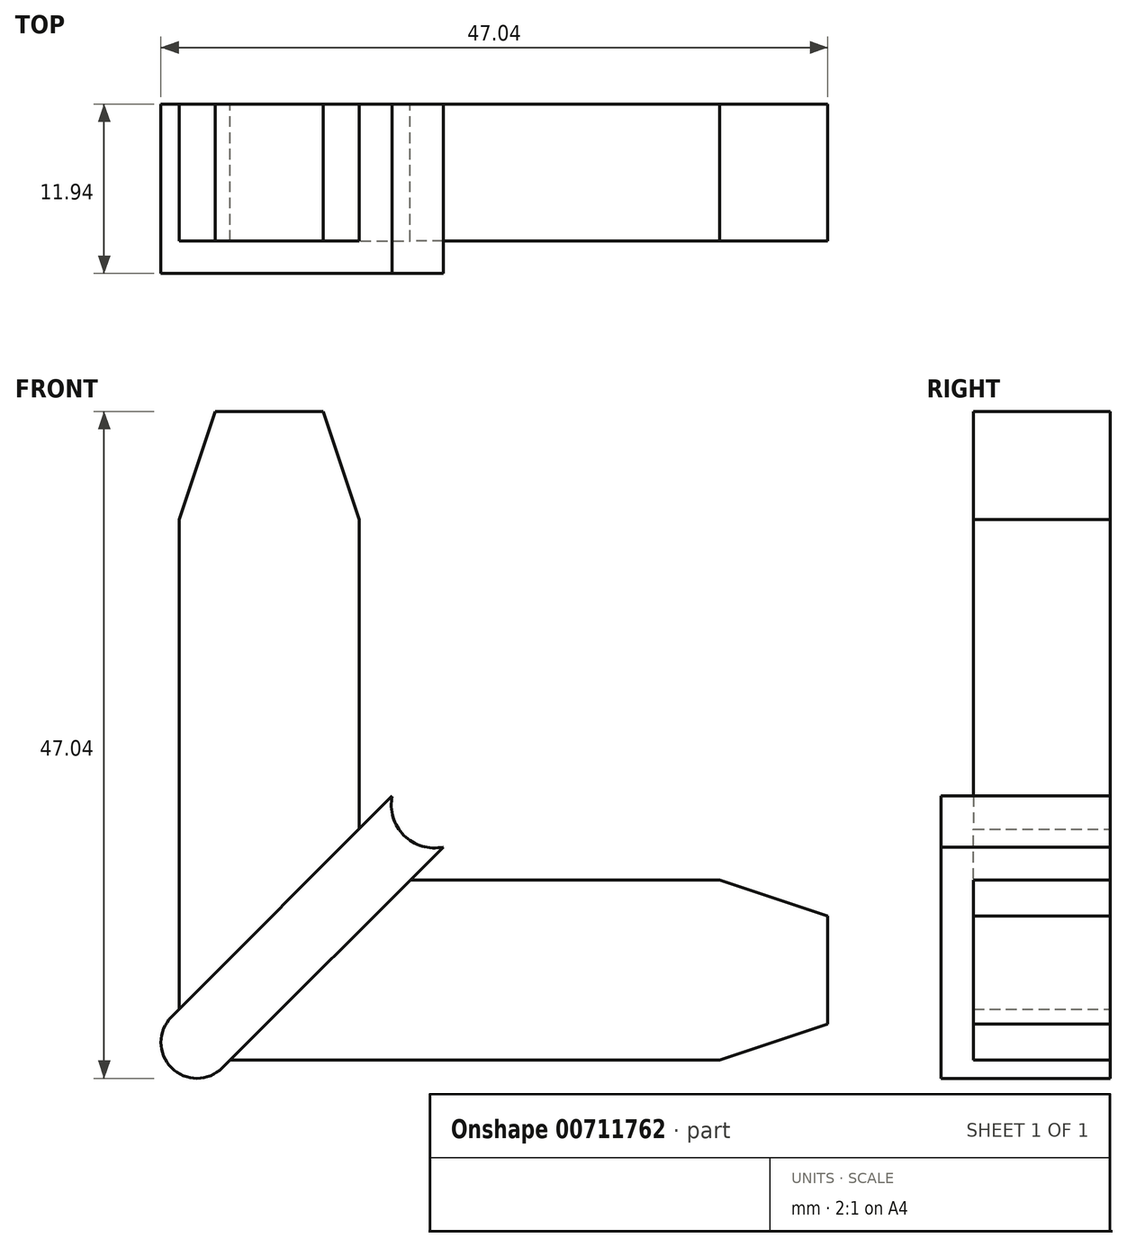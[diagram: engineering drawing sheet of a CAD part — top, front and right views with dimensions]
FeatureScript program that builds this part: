
annotation { "Feature Type Name" : "Feature", "Feature Type Description" : "" }
export const myFeature = defineFeature(function(context is Context, id is Id, definition is map)
    precondition{}
    {
        {
            var Q0;
            Q0=qCreatedBy(makeId("Front.planeOp"),FACE);
            var sketch = newSketch(context, id + "F0", { "sketchPlane" : qUnion([Q0])});
            skLineSegment(sketch, "E0.bottom", {"start": v(-4.55, -8.15) * mm, "end": v(37.61, -8.15) * mm});
            skLineSegment(sketch, "E0.right", {"start": v(37.61, -8.15) * mm, "end": v(37.61, 0) * mm});
            skPoint(sketch, "E0.middle", {"position": v(27.24, 0) * mm});
            skLineSegment(sketch, "E1.bottom", {"start": v(-6.89, -10.48) * mm, "end": v(10.48, 6.89) * mm});
            skLineSegment(sketch, "E1.top", {"start": v(-10.48, -6.89) * mm, "end": v(6.89, 10.48) * mm});
            skLineSegment(sketch, "E1.left", {"start": v(-6.89, -10.48) * mm, "end": v(-10.48, -6.89) * mm});
            skLineSegment(sketch, "E1.right", {"start": v(10.48, 6.89) * mm, "end": v(6.89, 10.48) * mm});
            skPoint(sketch, "E1.middle", {"position": v(0, 0) * mm});
            skLineSegment(sketch, "E2", {"start": v(0, 0) * mm, "end": v(15.93, 15.93) * mm, "construction": true});
            skLineSegment(sketch, "E3", {"start": v(37.61, 0) * mm, "end": v(37.61, 4.55) * mm});
            skLineSegment(sketch, "E4", {"start": v(37.61, 4.55) * mm, "end": v(8.15, 4.55) * mm});
            skLineSegment(sketch, "E5.MirrorCS", {"start": v(4.55, 37.61) * mm, "end": v(4.55, 8.15) * mm});
            skLineSegment(sketch, "E6.MirrorCS", {"start": v(-8.15, 37.61) * mm, "end": v(0, 37.61) * mm});
            skLineSegment(sketch, "E7.MirrorCS", {"start": v(-8.15, -4.55) * mm, "end": v(-8.15, 37.61) * mm});
            skLineSegment(sketch, "E8.MirrorCS", {"start": v(0, 37.61) * mm, "end": v(4.55, 37.61) * mm});
            skSolve(sketch);
        }
        {
            var Q0;
            {var subQ0=sQuery(id+"F0.wireOp",EDGE,"E1.left");Q0=makeQuery(id+"F0.imprint","IMPRINT",FACE,{"disambiguationData":[TD([[makeQuery(id+"F0.imprint","IMPRINT",EDGE,{"derivedFrom":subQ0}),-1.0]])]});}
            extrude(context, id + "F1", {"entities" : qUnion([Q0]), "depth" : 11.94 * mm, "offsetDistance" : 25.4 * mm});
        }
        {
            var Q0;
            {var subQ1=sQuery(id+"F0.wireOp",EDGE,"E5.MirrorCS");Q0=makeQuery(id+"F0.imprint","IMPRINT",FACE,{"disambiguationData":[TD([[makeQuery(id+"F0.imprint","IMPRINT",EDGE,{"derivedFrom":subQ1}),-1.0]])]});}
            var Q1;
            {var subQ1=sQuery(id+"F0.wireOp",EDGE,"E0.bottom");Q1=makeQuery(id+"F0.imprint","IMPRINT",FACE,{"disambiguationData":[TD([[makeQuery(id+"F0.imprint","IMPRINT",EDGE,{"derivedFrom":subQ1}),1.0]])]});}
            extrude(context, id + "F2", {"entities" : qUnion([Q0, Q1]), "operationType" : NewBodyOperationType.ADD, "depth" : 9.65 * mm, "offsetDistance" : 25.4 * mm});
        }
        {
            var Q0;
            Q0=makeQuery(id+"F2.opExtrude","SWEPT_EDGE",EDGE,{"disambiguationData":[OSD([sQuery(id+"F0.wireOp",EDGE,"E6.MirrorCS"),sQuery(id+"F0.wireOp",EDGE,"E7.MirrorCS")])]});
            var Q1;
            Q1=makeQuery(id+"F2.opExtrude","SWEPT_EDGE",EDGE,{"disambiguationData":[OSD([sQuery(id+"F0.wireOp",EDGE,"E5.MirrorCS"),sQuery(id+"F0.wireOp",EDGE,"E8.MirrorCS")])]});
            var Q2;
            Q2=makeQuery(id+"F2.opExtrude","SWEPT_EDGE",EDGE,{"disambiguationData":[OSD([sQuery(id+"F0.wireOp",EDGE,"E3"),sQuery(id+"F0.wireOp",EDGE,"E4")])]});
            chamfer(context, id + "F3", {"entities" : qUnion([Q0, Q1, Q2]), "chamferType" : ChamferType.TWO_OFFSETS, "width1" : 7.62 * mm, "oppositeDirection" : false, "width2" : 2.54 * mm, "tangentPropagation" : true});
        }
        {
            var Q0;
            Q0=makeQuery(id+"F2.opExtrude","SWEPT_EDGE",EDGE,{"disambiguationData":[OSD([sQuery(id+"F0.wireOp",EDGE,"E0.bottom"),sQuery(id+"F0.wireOp",EDGE,"E0.right")])]});
            chamfer(context, id + "F4", {"entities" : qUnion([Q0]), "chamferType" : ChamferType.TWO_OFFSETS, "width1" : 2.54 * mm, "oppositeDirection" : false, "width2" : 7.62 * mm, "tangentPropagation" : true});
        }
        {
            var Q0;
            Q0=makeQuery(id+"F1.opExtrude","SWEPT_EDGE",EDGE,{"disambiguationData":[OSD([sQuery(id+"F0.wireOp",EDGE,"E1.top"),sQuery(id+"F0.wireOp",EDGE,"E1.left")])]});
            var Q1;
            Q1=makeQuery(id+"F1.opExtrude","SWEPT_EDGE",EDGE,{"disambiguationData":[OSD([sQuery(id+"F0.wireOp",EDGE,"E1.bottom"),sQuery(id+"F0.wireOp",EDGE,"E1.left")])]});
            fillet(context, id + "F5", {"entities" : qUnion([Q0, Q1]), "radius" : 2.54 * mm, "tangentPropagation" : true, "allowEdgeOverflow" : false});
        }
        {
            var Q0;
            Q0=makeQuery(id+"F1.opExtrude","CAP_FACE",FACE,{"disambiguationData":[OSD([sQuery(id+"F0.wireOp",EDGE,"E1.bottom"),sQuery(id+"F0.wireOp",EDGE,"E1.top"),sQuery(id+"F0.wireOp",EDGE,"E1.left"),sQuery(id+"F0.wireOp",EDGE,"E1.right")])],"isStart":false});
            var sketch = newSketch(context, id + "F6", { "sketchPlane" : qUnion([Q0])});
            skCircle(sketch, "E9", {"center": v(9.86, 9.86) * mm, "radius": 3.04 * mm});
            skPoint(sketch, "E9.first.point", {"position": v(6.89, 10.48) * mm});
            skPoint(sketch, "E9.second.point", {"position": v(10.48, 6.89) * mm});
            skPoint(sketch, "E9.third.point", {"position": v(12.23, 11.77) * mm});
            skSolve(sketch);
        }
        {
            var Q0;
            Q0 = qSketchRegion(id + "F6", true);
            extrude(context, id + "F7", {"entities" : qUnion([Q0]), "operationType" : NewBodyOperationType.REMOVE, "oppositeDirection" : true, "depth" : 25.4 * mm, "offsetDistance" : 25.4 * mm});
        }
    });
